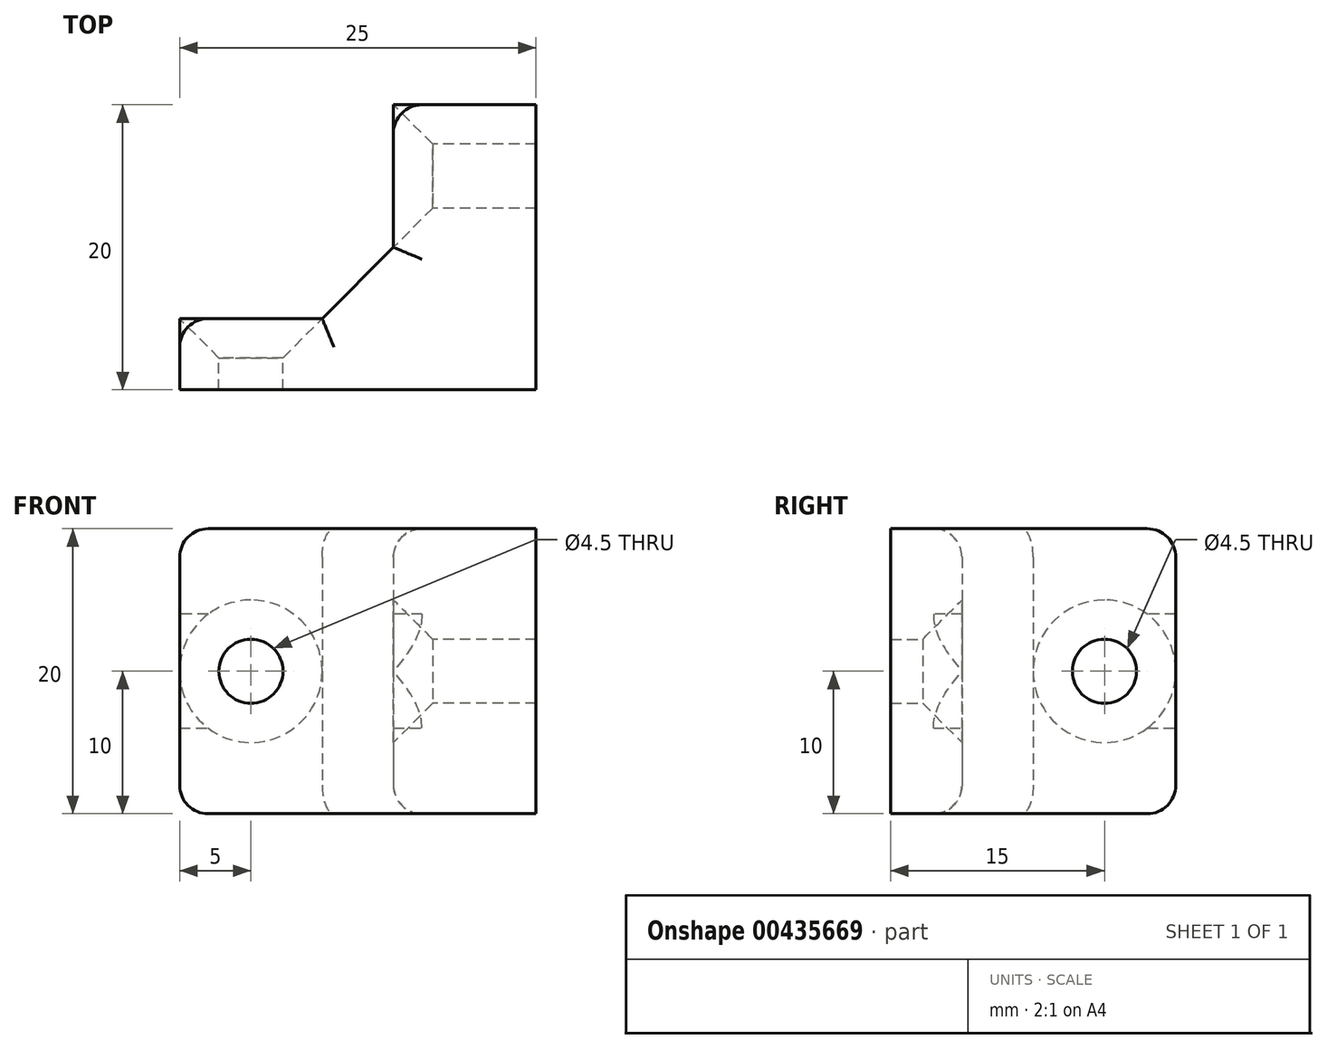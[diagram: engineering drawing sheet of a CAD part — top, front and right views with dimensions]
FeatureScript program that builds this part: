
annotation { "Feature Type Name" : "Feature", "Feature Type Description" : "" }
export const myFeature = defineFeature(function(context is Context, id is Id, definition is map)
    precondition{}
    {
        {
            var Q0;
            Q0=qCreatedBy(makeId("Top.planeOp"),FACE);
            var sketch = newSketch(context, id + "F0", { "sketchPlane" : qUnion([Q0])});
            skLineSegment(sketch, "E0", {"start": v(0, 0) * mm, "end": v(25, 0) * mm});
            skLineSegment(sketch, "E1", {"start": v(25, 0) * mm, "end": v(25, 20) * mm});
            skLineSegment(sketch, "E2", {"start": v(25, 20) * mm, "end": v(15, 20) * mm});
            skLineSegment(sketch, "E3", {"start": v(15, 20) * mm, "end": v(15, 10) * mm});
            skLineSegment(sketch, "E4", {"start": v(15, 10) * mm, "end": v(10, 5) * mm});
            skLineSegment(sketch, "E5", {"start": v(10, 5) * mm, "end": v(0, 5) * mm});
            skLineSegment(sketch, "E6", {"start": v(0, 5) * mm, "end": v(0, 0) * mm});
            skSolve(sketch);
        }
        {
            var Q0;
            Q0 = qSketchRegion(id + "F0", true);
            extrude(context, id + "F1", {"entities" : qUnion([Q0]), "depth" : 20 * mm});
        }
        {
            var Q0;
            Q0=makeQuery(id+"F1.opExtrude","SWEPT_FACE",FACE,{"disambiguationData":[OSD([sQuery(id+"F0.wireOp",EDGE,"E3")])]});
            var sketch = newSketch(context, id + "F2", { "sketchPlane" : qUnion([Q0])});
            skCircle(sketch, "E7", {"center": v(-15, 10) * mm, "radius": 2 * mm});
            skSolve(sketch);
        }
        {
            var Q0;
            Q0=makeQuery(id+"F1.opExtrude","SWEPT_FACE",FACE,{"disambiguationData":[OSD([sQuery(id+"F0.wireOp",EDGE,"E5")])]});
            var sketch = newSketch(context, id + "F3", { "sketchPlane" : qUnion([Q0])});
            skCircle(sketch, "E8", {"center": v(-5, 10) * mm, "radius": 2 * mm});
            skSolve(sketch);
        }
        {
            var Q0;
            Q0=sQuery(id+"F3.wireOp",VERTEX,"E8.center");
            var Q1;
            Q1=sQuery(id+"F2.wireOp",VERTEX,"E7.center");
            var Q2;
            Q2=makeQuery(id+"F1.opExtrude","SWEPT_BODY",BODY,{"disambiguationData":[OSD([sQuery(id+"F0.wireOp",EDGE,"E0"),sQuery(id+"F0.wireOp",EDGE,"E1"),sQuery(id+"F0.wireOp",EDGE,"E2"),sQuery(id+"F0.wireOp",EDGE,"E3"),sQuery(id+"F0.wireOp",EDGE,"E4"),sQuery(id+"F0.wireOp",EDGE,"E5"),sQuery(id+"F0.wireOp",EDGE,"E6")])]});
            hole(context, id + "F4", {"style" : HoleStyle.C_SINK, "endStyle" : HoleEndStyle.THROUGH, "holeDiameter" : 4.5 * mm, "cSinkDiameter" : 10 * mm, "cSinkAngle" : 90 * degree, "isTappedThrough" : true, "tappedDepth" : 12.7 * mm, "tapClearance" : 3, "locations" : qUnion([Q0, Q1]), "scope" : qUnion([Q2])});
        }
        {
            var Q0;
            {var subQ0=sQuery(id+"F0.wireOp",EDGE,"E6");var subQ1=sQuery(id+"F0.wireOp",EDGE,"E5");Q0=makeQuery(id+"F4.hole-0.boolean.opBoolean","SPLIT",EDGE,{"disambiguationData":[TD([makeQuery(id+"F1.opExtrude","CAP_FACE",FACE,{"disambiguationData":[OSD([sQuery(id+"F0.wireOp",EDGE,"E0"),sQuery(id+"F0.wireOp",EDGE,"E1"),sQuery(id+"F0.wireOp",EDGE,"E2"),sQuery(id+"F0.wireOp",EDGE,"E3"),sQuery(id+"F0.wireOp",EDGE,"E4"),subQ1,subQ0])],"isStart":false})])],"derivedFrom":makeQuery(id+"F1.opExtrude","SWEPT_EDGE",EDGE,{"disambiguationData":[OSD([subQ1,subQ0])]})});}
            var Q1;
            Q1=makeQuery(id+"F1.opExtrude","CAP_EDGE",EDGE,{"disambiguationData":[OSD([sQuery(id+"F0.wireOp",EDGE,"E5")])],"isStart":false});
            var Q2;
            Q2=makeQuery(id+"F1.opExtrude","CAP_EDGE",EDGE,{"disambiguationData":[OSD([sQuery(id+"F0.wireOp",EDGE,"E4")])],"isStart":false});
            var Q3;
            Q3=makeQuery(id+"F1.opExtrude","CAP_EDGE",EDGE,{"disambiguationData":[OSD([sQuery(id+"F0.wireOp",EDGE,"E3")])],"isStart":false});
            var Q4;
            {var subQ0=sQuery(id+"F0.wireOp",EDGE,"E3");var subQ1=sQuery(id+"F0.wireOp",EDGE,"E2");Q4=makeQuery(id+"F4.hole-1.boolean.opBoolean","SPLIT",EDGE,{"disambiguationData":[TD([makeQuery(id+"F1.opExtrude","CAP_FACE",FACE,{"disambiguationData":[OSD([sQuery(id+"F0.wireOp",EDGE,"E0"),sQuery(id+"F0.wireOp",EDGE,"E1"),subQ1,subQ0,sQuery(id+"F0.wireOp",EDGE,"E4"),sQuery(id+"F0.wireOp",EDGE,"E5"),sQuery(id+"F0.wireOp",EDGE,"E6")])],"isStart":false})])],"derivedFrom":makeQuery(id+"F1.opExtrude","SWEPT_EDGE",EDGE,{"disambiguationData":[OSD([subQ1,subQ0])]})});}
            var Q5;
            Q5=makeQuery(id+"F1.opExtrude","CAP_EDGE",EDGE,{"disambiguationData":[OSD([sQuery(id+"F0.wireOp",EDGE,"E3")])],"isStart":true});
            var Q6;
            Q6=makeQuery(id+"F1.opExtrude","CAP_EDGE",EDGE,{"disambiguationData":[OSD([sQuery(id+"F0.wireOp",EDGE,"E4")])],"isStart":true});
            var Q7;
            Q7=makeQuery(id+"F1.opExtrude","CAP_EDGE",EDGE,{"disambiguationData":[OSD([sQuery(id+"F0.wireOp",EDGE,"E5")])],"isStart":true});
            var Q8;
            {var subQ0=sQuery(id+"F0.wireOp",EDGE,"E6");var subQ1=sQuery(id+"F0.wireOp",EDGE,"E5");Q8=makeQuery(id+"F4.hole-0.boolean.opBoolean","SPLIT",EDGE,{"disambiguationData":[TD([makeQuery(id+"F1.opExtrude","CAP_FACE",FACE,{"disambiguationData":[OSD([sQuery(id+"F0.wireOp",EDGE,"E0"),sQuery(id+"F0.wireOp",EDGE,"E1"),sQuery(id+"F0.wireOp",EDGE,"E2"),sQuery(id+"F0.wireOp",EDGE,"E3"),sQuery(id+"F0.wireOp",EDGE,"E4"),subQ1,subQ0])],"isStart":true})])],"derivedFrom":makeQuery(id+"F1.opExtrude","SWEPT_EDGE",EDGE,{"disambiguationData":[OSD([subQ1,subQ0])]})});}
            var Q9;
            {var subQ0=sQuery(id+"F0.wireOp",EDGE,"E3");var subQ1=sQuery(id+"F0.wireOp",EDGE,"E2");Q9=makeQuery(id+"F4.hole-1.boolean.opBoolean","SPLIT",EDGE,{"disambiguationData":[TD([makeQuery(id+"F1.opExtrude","CAP_FACE",FACE,{"disambiguationData":[OSD([sQuery(id+"F0.wireOp",EDGE,"E0"),sQuery(id+"F0.wireOp",EDGE,"E1"),subQ1,subQ0,sQuery(id+"F0.wireOp",EDGE,"E4"),sQuery(id+"F0.wireOp",EDGE,"E5"),sQuery(id+"F0.wireOp",EDGE,"E6")])],"isStart":true})])],"derivedFrom":makeQuery(id+"F1.opExtrude","SWEPT_EDGE",EDGE,{"disambiguationData":[OSD([subQ1,subQ0])]})});}
            var Q10;
            Q10=makeQuery(id+"F1.opExtrude","CAP_EDGE",EDGE,{"disambiguationData":[OSD([sQuery(id+"F0.wireOp",EDGE,"E2")])],"isStart":false});
            var Q11;
            Q11=makeQuery(id+"F1.opExtrude","CAP_EDGE",EDGE,{"disambiguationData":[OSD([sQuery(id+"F0.wireOp",EDGE,"E6")])],"isStart":false});
            var Q12;
            Q12=makeQuery(id+"F1.opExtrude","CAP_EDGE",EDGE,{"disambiguationData":[OSD([sQuery(id+"F0.wireOp",EDGE,"E6")])],"isStart":true});
            var Q13;
            Q13=makeQuery(id+"F1.opExtrude","CAP_EDGE",EDGE,{"disambiguationData":[OSD([sQuery(id+"F0.wireOp",EDGE,"E2")])],"isStart":true});
            fillet(context, id + "F5", {"entities" : qUnion([Q0, Q1, Q2, Q3, Q4, Q5, Q6, Q7, Q8, Q9, Q10, Q11, Q12, Q13]), "radius" : 2 * mm, "tangentPropagation" : true, "allowEdgeOverflow" : false});
        }
    });
